# Revit family: Haworth_EncloseFrameless_Door_DoubleSliding
name_source: partatom
category: Furniture Systems
revit_build: Autodesk Revit 2018 (Build: 20170223_1515(x64)
units: mm (PartAtom-declared; Revit-internal decimal feet)

## family parameters
Always vertical = Yes
Cut with Voids When Loaded = No
OmniClass Number = 23.25.40.14
OmniClass Title = Demountable Partitions
Part Type = Normal
Room Calculation Point = No
Round Connector Dimension = Use Diameter
Shared = Yes
Work Plane-Based = No

## types (4) — shared parameters
Actual Door Height = 107 "
Actual Height = 108 "
Assembly Code = C1010200
Cap Height = 1 "
Ceiling Mount = Yes
Description = Door - Double Sliding
Door Hardware Finish = Haworth _ Metal _ Brushed Aluminum
Door Height = 107 "
Door Pull Length = 16 "
Door Pull Offset = 1.66 "
End of Run Finish = Haworth _ Polymer _ Black
End of Run Width = 0.155 "
Frame Depth = 4 "
Frame Finish = Haworth _ Metal _ Brushed Aluminum
Glass Depth = 0.4 "
Glass Finish = Haworth _ Glass _ Clear
Height = 108 "
Horizontal Frame Width = 0.875 "
Horizontal Top Adjuster Width = 2.625 "
Horizontal Top Trim Width = 1.5 "
Manufacturer = Haworth
Material Options = http://surfaces.haworth.com
Max. Height = 120 "
Max. Width = 96 "
Min. Height = 84 "
Min. Width = 48 "
Min/Max Height = 108-144 in.
Min/Max Width = 48-96 in.
Model = Haworth - Enclose Frameless
Pull Height Centerline = 40 "
Pull Offset Centerline = 2.755 "
Rectilinear D Pull = No
Revision Number = 3
Size = Verify Final Dim. w/ Haworth
Sustainability Info = http://www.haworth.com
Tubular D Pull = Yes
URL = www.haworth.com
URL - Product = http://www.haworth.com
Vertical Frame Width = 0.875 "
Warranty = http://www.haworth.com

## per-type parameters (varying)
| type | Actual Door Width | Actual Width | Door Leaf Width | Overall Door Opening | Sliding Track Length | Width |
| 72" x 108" | 35.845 " | 72 " | 35.845 " | 71.69 " | 34.97 " | 72 " |
| 48" x 108" | 23.845 " | 48 " | 23.845 " | 47.69 " | 22.97 " | 48 " |
| 60" x 108" | 29.845 " | 60 " | 29.845 " | 59.69 " | 28.97 " | 60 " |
| 96" x 108" | 47.845 " | 96 " | 47.845 " | 95.69 " | 46.97 " | 96 " |

## geometry (parser evidence)
native form markers: Blend x4, Sweep x14
no freeform markers — native parametric forms only
